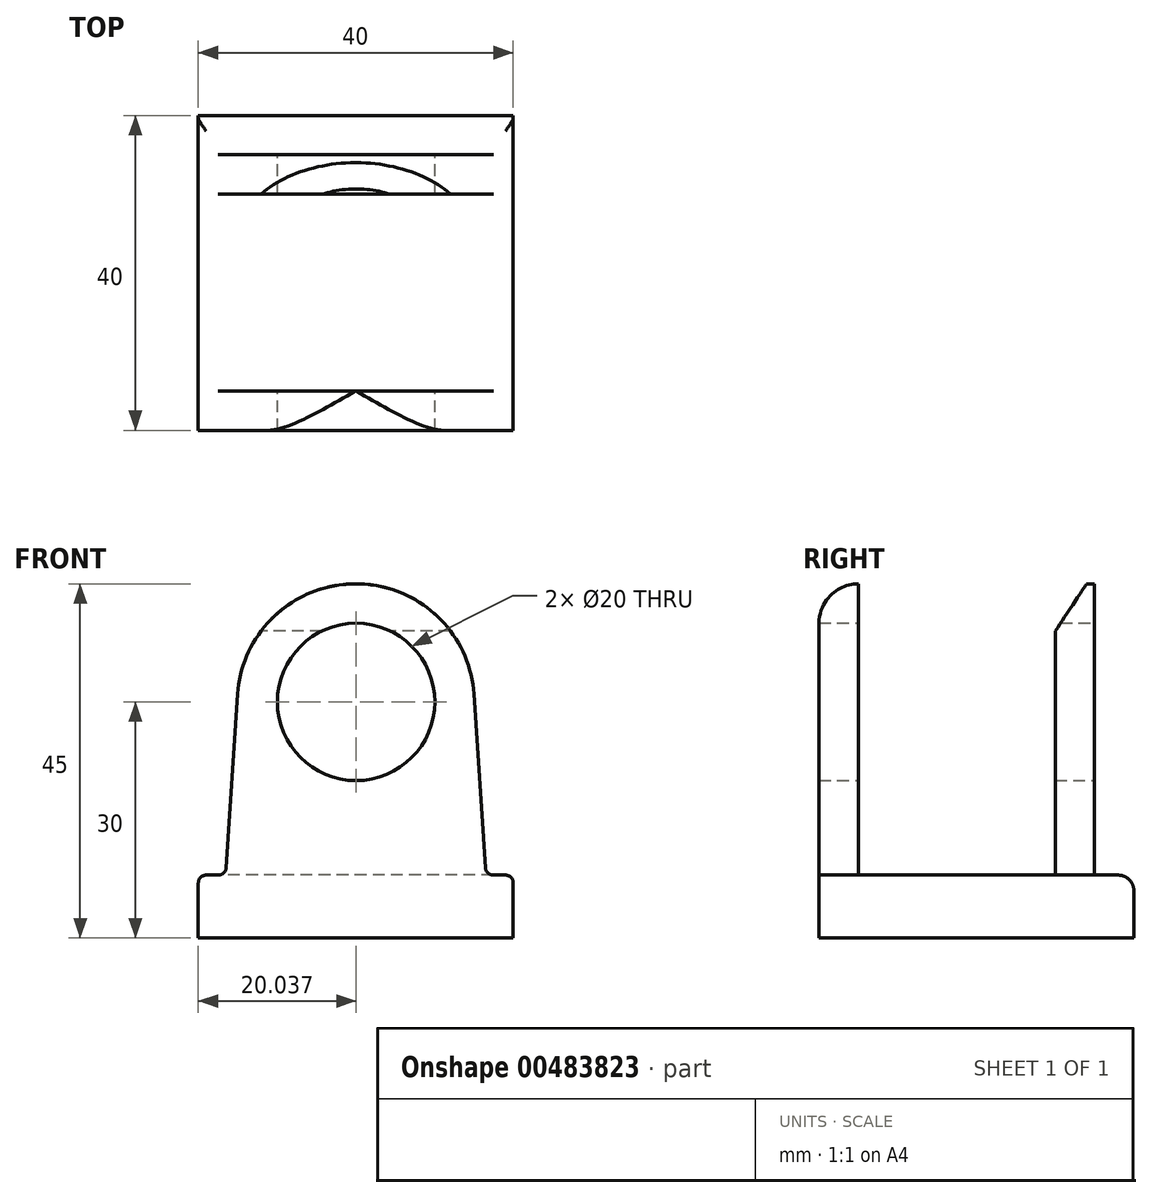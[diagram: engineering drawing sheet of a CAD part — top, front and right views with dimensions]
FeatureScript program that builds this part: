
annotation { "Feature Type Name" : "Feature", "Feature Type Description" : "" }
export const myFeature = defineFeature(function(context is Context, id is Id, definition is map)
    precondition{}
    {
        {
            var Q0;
            Q0=qCreatedBy(makeId("Front.planeOp"),FACE);
            var sketch = newSketch(context, id + "F0", { "sketchPlane" : qUnion([Q0])});
            skLineSegment(sketch, "E0.bottom", {"start": v(20, -4) * mm, "end": v(-20, -4) * mm});
            skLineSegment(sketch, "E0.top", {"start": v(19, 4) * mm, "end": v(17.47, 4) * mm});
            skLineSegment(sketch, "E0.left", {"start": v(20, -4) * mm, "end": v(20, 3) * mm});
            skLineSegment(sketch, "E0.right", {"start": v(-20, -4) * mm, "end": v(-20, 3) * mm});
            skPoint(sketch, "E0.middle", {"position": v(0, 0) * mm});
            skLineSegment(sketch, "E1", {"start": v(-16.47, 4.93) * mm, "end": v(-15, 27) * mm});
            skArc(sketch, "E2", {"start": v(-15, 27) * mm, "mid": v(-10.27, 36.96) * mm, "end": v(0, 41) * mm});
            skLineSegment(sketch, "E3", {"start": v(0, -4) * mm, "end": v(-0.04, 26) * mm});
            skLineSegment(sketch, "E4.MirrorCS", {"start": v(16.47, 4.93) * mm, "end": v(15, 27) * mm});
            skArc(sketch, "E5.MirrorCS", {"start": v(15, 27) * mm, "mid": v(10.27, 36.96) * mm, "end": v(0, 41) * mm});
            skCircle(sketch, "E6", {"center": v(0.04, 26) * mm, "radius": 10 * mm});
            skCircle(sketch, "E7", {"center": v(0.04, 26) * mm, "radius": 5 * mm});
            skLineSegment(sketch, "E8", {"start": v(-17.47, 4) * mm, "end": v(-19, 4) * mm});
            skLineSegment(sketch, "E9", {"start": v(16.53, 4) * mm, "end": v(-16.53, 4) * mm});
            skPoint(sketch, "E10.visualSharp", {"position": v(-16.53, 4) * mm});
            skArc(sketch, "E10.filletArc", {"start": v(-17.47, 4) * mm, "mid": v(-16.78, 4.27) * mm, "end": v(-16.47, 4.93) * mm});
            skPoint(sketch, "E11.visualSharp", {"position": v(16.53, 4) * mm});
            skArc(sketch, "E11.filletArc", {"start": v(16.47, 4.93) * mm, "mid": v(16.78, 4.27) * mm, "end": v(17.47, 4) * mm});
            skPoint(sketch, "E12.visualSharp", {"position": v(-20, 4) * mm});
            skArc(sketch, "E12.filletArc", {"start": v(-19, 4) * mm, "mid": v(-19.7, 3.7) * mm, "end": v(-20, 3) * mm});
            skPoint(sketch, "E13.visualSharp", {"position": v(20, 4) * mm});
            skArc(sketch, "E13.filletArc", {"start": v(20, 3) * mm, "mid": v(19.7, 3.7) * mm, "end": v(19, 4) * mm});
            skSolve(sketch);
        }
        {
            var Q0;
            Q0=qCreatedBy(makeId("Right.planeOp"),FACE);
            var sketch = newSketch(context, id + "F1", { "sketchPlane" : qUnion([Q0])});
            skLineSegment(sketch, "E14.bottom", {"start": v(18, 4) * mm, "end": v(14, 4) * mm});
            skLineSegment(sketch, "E14.top", {"start": v(20, -4) * mm, "end": v(20, -4) * mm});
            skLineSegment(sketch, "E14.left", {"start": v(20, 2) * mm, "end": v(20, -4) * mm});
            skLineSegment(sketch, "E14.right", {"start": v(-20, 4) * mm, "end": v(-20, -4) * mm});
            skPoint(sketch, "E14.middle", {"position": v(0, 0) * mm});
            skLineSegment(sketch, "E15.bottom", {"start": v(-20, 4) * mm, "end": v(-15, 4) * mm});
            skLineSegment(sketch, "E15.top", {"start": v(-15, 41) * mm, "end": v(-15, 41) * mm});
            skLineSegment(sketch, "E15.left", {"start": v(-20, 4) * mm, "end": v(-20, 41) * mm});
            skLineSegment(sketch, "E15.right", {"start": v(-15, 4) * mm, "end": v(-15, 41) * mm});
            skLineSegment(sketch, "E16", {"start": v(-20, 36) * mm, "end": v(-20, 36) * mm});
            skPoint(sketch, "E17.visualSharp", {"position": v(-20, 41) * mm});
            skArc(sketch, "E17.filletArc", {"start": v(-15, 41) * mm, "mid": v(-18.54, 39.54) * mm, "end": v(-20, 36) * mm});
            skPoint(sketch, "E18.visualSharp", {"position": v(20, 4) * mm});
            skArc(sketch, "E18.filletArc", {"start": v(20, 2) * mm, "mid": v(19.41, 3.41) * mm, "end": v(18, 4) * mm});
            skLineSegment(sketch, "E19", {"start": v(20, 4) * mm, "end": v(15, 4) * mm});
            skLineSegment(sketch, "E20.bottom", {"start": v(15, 4) * mm, "end": v(14, 4) * mm});
            skLineSegment(sketch, "E20.top", {"start": v(15, 41) * mm, "end": v(14.5, 41) * mm});
            skLineSegment(sketch, "E20.left", {"start": v(15, 4) * mm, "end": v(15, 4) * mm});
            skLineSegment(sketch, "E21", {"start": v(15, 41) * mm, "end": v(14, 41) * mm});
            skLineSegment(sketch, "E22", {"start": v(14.5, 41) * mm, "end": v(14, 41) * mm});
            skLineSegment(sketch, "E23", {"start": v(15, 41) * mm, "end": v(15, 41) * mm});
            skLineSegment(sketch, "E24", {"start": v(14, 4) * mm, "end": v(14, 4) * mm});
            skLineSegment(sketch, "E25", {"start": v(20, -4) * mm, "end": v(-20, -4) * mm});
            skLineSegment(sketch, "E26", {"start": v(14, 41) * mm, "end": v(14, 41) * mm});
            skLineSegment(sketch, "E27", {"start": v(14, 4) * mm, "end": v(10, 4) * mm});
            skLineSegment(sketch, "E28", {"start": v(10, 4) * mm, "end": v(10, 35) * mm});
            skLineSegment(sketch, "E29", {"start": v(10, 35) * mm, "end": v(14, 41) * mm});
            skLineSegment(sketch, "E30", {"start": v(15, 4) * mm, "end": v(15, 41) * mm});
            skLineSegment(sketch, "E31", {"start": v(10, 4) * mm, "end": v(-20, 4) * mm});
            skSolve(sketch);
        }
        {
            var Q0;
            Q0 = qSketchRegion(id + "F0", true);
            extrude(context, id + "F2", {"entities" : qUnion([Q0]), "depth" : 20 * mm, "hasSecondDirection" : true, "secondDirectionOppositeDirection" : true, "secondDirectionDepth" : 20 * mm});
        }
        {
            var Q0;
            Q0 = qSketchRegion(id + "F1", true);
            extrude(context, id + "F3", {"entities" : qUnion([Q0]), "operationType" : NewBodyOperationType.INTERSECT, "depth" : 34.04 * mm, "hasSecondDirection" : true, "secondDirectionOppositeDirection" : true, "secondDirectionDepth" : 25.4 * mm});
        }
    });
